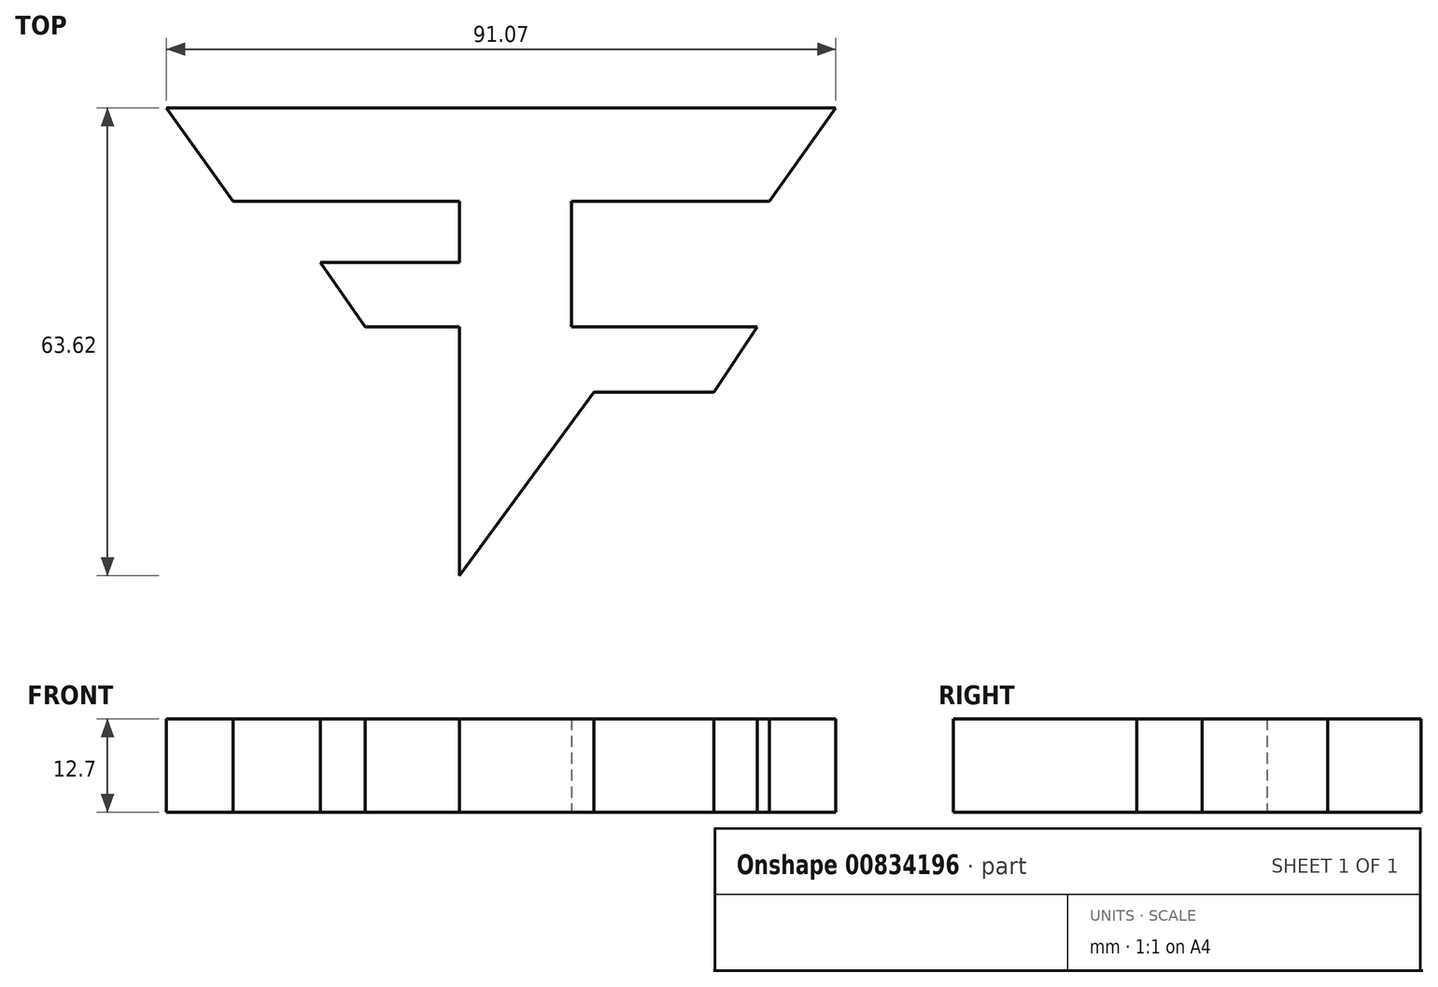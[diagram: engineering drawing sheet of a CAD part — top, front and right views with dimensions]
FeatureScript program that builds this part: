
annotation { "Feature Type Name" : "Feature", "Feature Type Description" : "" }
export const myFeature = defineFeature(function(context is Context, id is Id, definition is map)
    precondition{}
    {
        {
            var Q0;
            Q0=qCreatedBy(makeId("Top.planeOp"),FACE);
            var sketch = newSketch(context, id + "F0", { "sketchPlane" : qUnion([Q0])});
            skLineSegment(sketch, "E0.bottom", {"start": v(-42.3, 54.16) * mm, "end": v(48.76, 54.16) * mm});
            skLineSegment(sketch, "E0.top", {"start": v(-33.27, 41.46) * mm, "end": v(-2.45, 41.46) * mm});
            skLineSegment(sketch, "E1.left", {"start": v(-2.45, 41.46) * mm, "end": v(-2.45, 33.16) * mm});
            skLineSegment(sketch, "E1.right", {"start": v(12.8, 41.46) * mm, "end": v(12.8, 24.37) * mm});
            skLineSegment(sketch, "E2.bottom", {"start": v(-2.45, 33.16) * mm, "end": v(-21.35, 33.16) * mm});
            skLineSegment(sketch, "E2.top", {"start": v(-2.45, 24.37) * mm, "end": v(-15.3, 24.37) * mm});
            skLineSegment(sketch, "E3", {"start": v(-42.3, 54.16) * mm, "end": v(-33.27, 41.46) * mm});
            skLineSegment(sketch, "E4", {"start": v(48.76, 54.16) * mm, "end": v(39.7, 41.46) * mm});
            skLineSegment(sketch, "E5", {"start": v(-21.35, 33.16) * mm, "end": v(-15.3, 24.37) * mm});
            skLineSegment(sketch, "E6.trimOffspring", {"start": v(12.8, 41.46) * mm, "end": v(39.7, 41.46) * mm});
            skLineSegment(sketch, "E7.bottom", {"start": v(12.8, 24.37) * mm, "end": v(38.05, 24.37) * mm});
            skLineSegment(sketch, "E7.top", {"start": v(22.47, 15.48) * mm, "end": v(32.15, 15.48) * mm});
            skLineSegment(sketch, "E8", {"start": v(38.05, 24.37) * mm, "end": v(32.15, 15.48) * mm});
            skLineSegment(sketch, "E9", {"start": v(-2.45, 24.37) * mm, "end": v(-2.45, 0) * mm});
            skLineSegment(sketch, "E10", {"start": v(-2.45, -9.46) * mm, "end": v(-2.45, 0) * mm});
            skLineSegment(sketch, "E11", {"start": v(22.47, 15.48) * mm, "end": v(15.86, 15.48) * mm});
            skLineSegment(sketch, "E12", {"start": v(15.86, 15.48) * mm, "end": v(-2.45, -9.46) * mm});
            skSolve(sketch);
        }
        {
            var Q0;
            Q0=makeQuery(id+"F0.imprint","IMPRINT",FACE,{"disambiguationData":[TD([[makeQuery(id+"F0.imprint","IMPRINT",EDGE,{"derivedFrom":sQuery(id+"F0.wireOp",EDGE,"E0.bottom")}),-1.0]])]});
            extrude(context, id + "F1", {"entities" : qUnion([Q0]), "depth" : 12.7 * mm, "offsetDistance" : 25.4 * mm});
        }
    });
